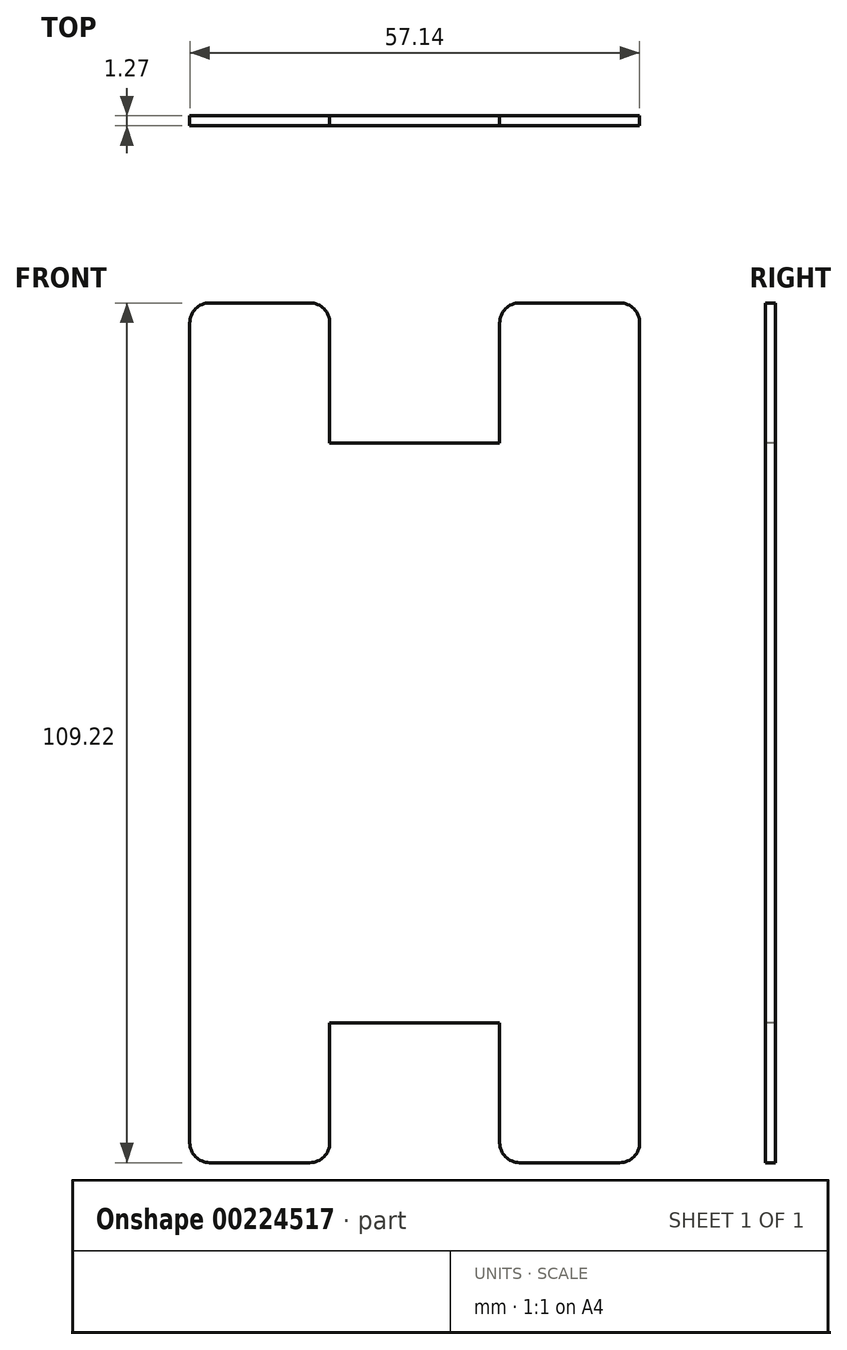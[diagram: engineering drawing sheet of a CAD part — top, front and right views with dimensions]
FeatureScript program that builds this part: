
annotation { "Feature Type Name" : "Feature", "Feature Type Description" : "" }
export const myFeature = defineFeature(function(context is Context, id is Id, definition is map)
    precondition{}
    {
        {
            var Q0;
            Q0=qCreatedBy(makeId("Front.planeOp"),FACE);
            var sketch = newSketch(context, id + "F0", { "sketchPlane" : qUnion([Q0])});
            skLineSegment(sketch, "E0.bottom", {"start": v(-26.04, 54.6) * mm, "end": v(-13.34, 54.6) * mm});
            skLineSegment(sketch, "E0.top", {"start": v(-26.04, -54.61) * mm, "end": v(-13.34, -54.61) * mm});
            skLineSegment(sketch, "E0.left", {"start": v(-28.57, 52.07) * mm, "end": v(-28.58, -52.07) * mm});
            skLineSegment(sketch, "E0.right", {"start": v(28.58, 52.07) * mm, "end": v(28.57, -52.07) * mm});
            skPoint(sketch, "E0.middle", {"position": v(0, 0) * mm});
            skLineSegment(sketch, "E1", {"start": v(13.33, 54.6) * mm, "end": v(26.03, 54.6) * mm});
            skLineSegment(sketch, "E2", {"start": v(-10.8, 52.07) * mm, "end": v(-10.8, 36.83) * mm});
            skLineSegment(sketch, "E3", {"start": v(-10.8, 36.83) * mm, "end": v(10.8, 36.83) * mm});
            skLineSegment(sketch, "E4", {"start": v(10.8, 36.83) * mm, "end": v(10.8, 52.07) * mm});
            skLineSegment(sketch, "E5.MirrorCS", {"start": v(-10.8, -36.83) * mm, "end": v(10.8, -36.83) * mm});
            skLineSegment(sketch, "E6.MirrorCS", {"start": v(10.8, -36.83) * mm, "end": v(10.8, -52.07) * mm});
            skLineSegment(sketch, "E7.MirrorCS", {"start": v(-10.8, -52.07) * mm, "end": v(-10.8, -36.83) * mm});
            skLineSegment(sketch, "E8", {"start": v(13.33, -54.61) * mm, "end": v(26.03, -54.61) * mm});
            skPoint(sketch, "E9.visualSharp", {"position": v(-28.58, -54.61) * mm});
            skArc(sketch, "E9.filletArc", {"start": v(-28.58, -52.07) * mm, "mid": v(-27.83, -53.87) * mm, "end": v(-26.04, -54.61) * mm});
            skPoint(sketch, "E10.visualSharp", {"position": v(-10.8, -54.61) * mm});
            skArc(sketch, "E10.filletArc", {"start": v(-13.34, -54.61) * mm, "mid": v(-11.54, -53.87) * mm, "end": v(-10.8, -52.07) * mm});
            skPoint(sketch, "E11.visualSharp", {"position": v(28.57, -54.61) * mm});
            skArc(sketch, "E11.filletArc", {"start": v(26.03, -54.61) * mm, "mid": v(27.83, -53.87) * mm, "end": v(28.57, -52.07) * mm});
            skPoint(sketch, "E12.visualSharp", {"position": v(10.8, -54.61) * mm});
            skArc(sketch, "E12.filletArc", {"start": v(10.8, -52.07) * mm, "mid": v(11.54, -53.87) * mm, "end": v(13.33, -54.61) * mm});
            skPoint(sketch, "E13.visualSharp", {"position": v(10.8, 54.61) * mm});
            skArc(sketch, "E13.filletArc", {"start": v(13.33, 54.61) * mm, "mid": v(11.54, 53.87) * mm, "end": v(10.8, 52.07) * mm});
            skPoint(sketch, "E14.visualSharp", {"position": v(28.58, 54.6) * mm});
            skArc(sketch, "E14.filletArc", {"start": v(28.57, 52.07) * mm, "mid": v(27.83, 53.87) * mm, "end": v(26.03, 54.61) * mm});
            skPoint(sketch, "E15.visualSharp", {"position": v(-28.57, 54.6) * mm});
            skArc(sketch, "E15.filletArc", {"start": v(-26.04, 54.61) * mm, "mid": v(-27.83, 53.87) * mm, "end": v(-28.58, 52.07) * mm});
            skPoint(sketch, "E16.visualSharp", {"position": v(-10.8, 54.6) * mm});
            skArc(sketch, "E16.filletArc", {"start": v(-10.8, 52.07) * mm, "mid": v(-11.54, 53.87) * mm, "end": v(-13.34, 54.61) * mm});
            skSolve(sketch);
        }
        {
            var Q0;
            Q0=makeQuery(id+"F0.imprint","IMPRINT",FACE,{"disambiguationData":[TD([[makeQuery(id+"F0.imprint","IMPRINT",EDGE,{"derivedFrom":sQuery(id+"F0.wireOp",EDGE,"E0.bottom")}),-1.0]])]});
            extrude(context, id + "F1", {"entities" : qUnion([Q0]), "oppositeDirection" : true, "depth" : 1.27 * mm});
        }
    });
